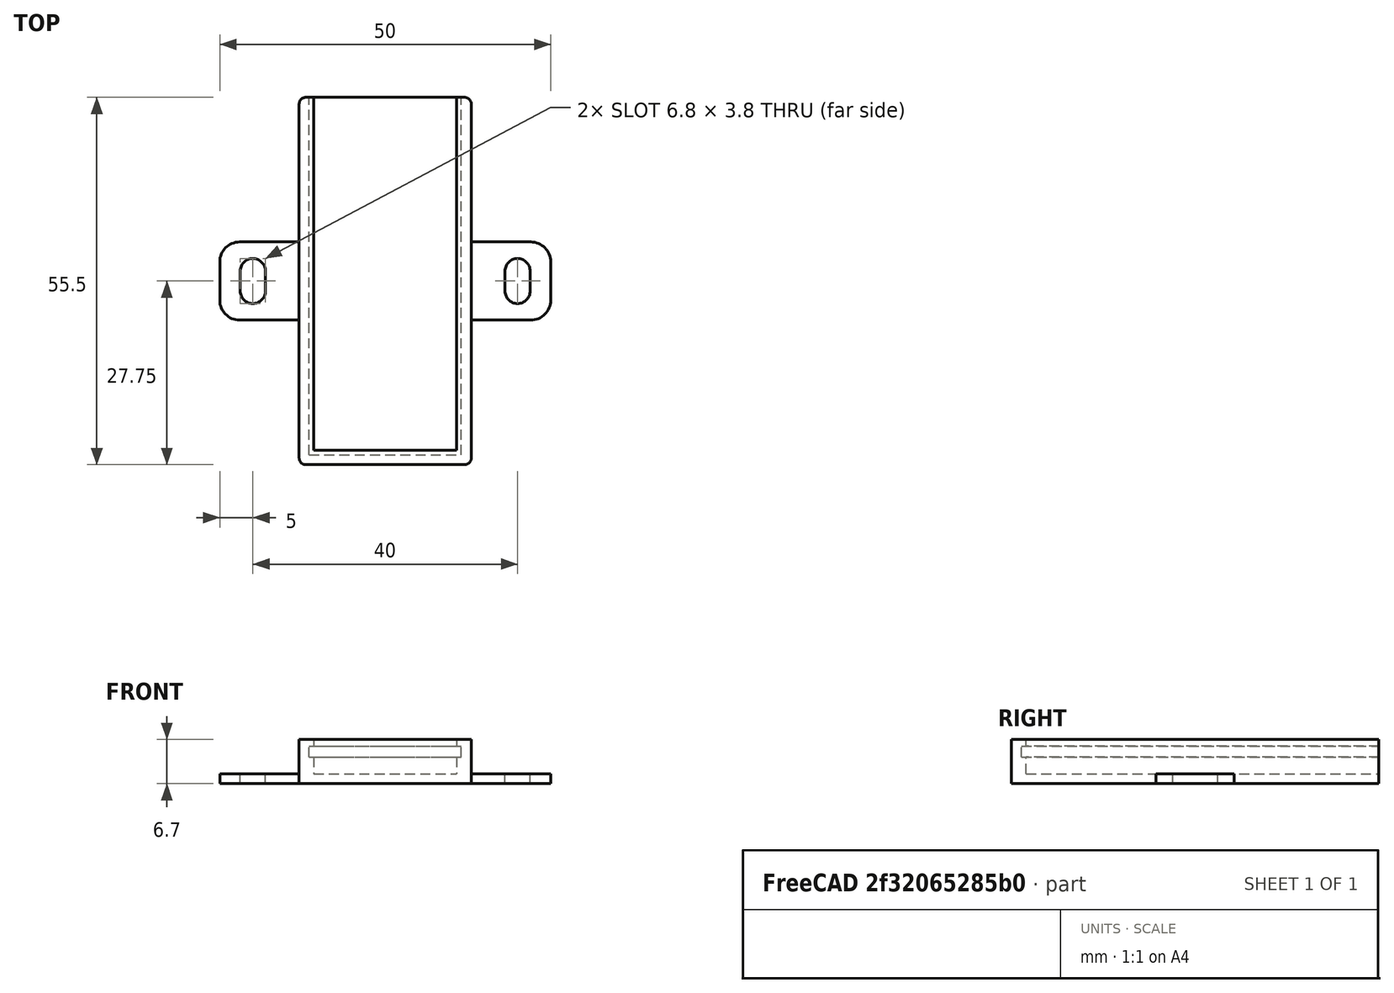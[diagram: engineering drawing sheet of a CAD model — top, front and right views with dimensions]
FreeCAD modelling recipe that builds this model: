
FCSTD DOCUMENT  (FreeCAD 0.19R)
Label: stm32_bluepill_2044l
License: FreeArt
LicenseURL: http://artlibre.org/licence/lal
objects: Part::Box×3, Part::MultiFuse×2, Part::Cut×2, App::Part×2, Spreadsheet::Sheet×1, Part::Fillet×1, Part::Feature×1
note: 9 computed .brp shape members not serialized (recipe doc carries the construction recipe); baked Part::Feature solids carry a one-line shape summary decoded from their .brp

FEATURE [Spreadsheet::Sheet] Spreadsheet  label="p"
  cells = A1=pcb_x; B1(pcb_x)=23; A2=pcb_y; B2(pcb_y)=54; A3=pcb_z; B3(pcb_z)=1.7; A4=pcb_under; B4(pcb_under)=2.5; A5=side_wall; B5(side_wall)=1.5; A6=pcb_side_lane; B6(pcb_side_lane)=0.7; A7=bottom_wall; B7(bottom_wall)=1.5; A8=pcb_above; B8(pcb_above)=1
FEATURE [Part::Box] Box  label="external cube"
  AttacherType = Attacher::AttachEngine3D
  Height = 6.7
  Length = 26
  Width = 55.5
  expr: Height = <<p>>.bottom_wall + <<p>>.pcb_under + <<p>>.pcb_z + <<p>>.pcb_above
  expr: Width = <<p>>.pcb_y + <<p>>.side_wall
  expr: Length = <<p>>.pcb_x + 2 * <<p>>.side_wall
FEATURE [Part::Box] Box006  label="internal cube"
  AttacherType = Attacher::AttachEngine3D
  Height = 5.2
  Length = 21.6
  Placement = pos=(2.2,2.2,1.5) rot=(0,0,1;0rad)
  Width = 54.1
  expr: .Placement.Base.y = <<p>>.side_wall + <<p>>.pcb_side_lane
  expr: .Placement.Base.x = <<p>>.side_wall + <<p>>.pcb_side_lane
  expr: .Placement.Base.z = <<p>>.bottom_wall
  expr: Height = <<p>>.pcb_under + <<p>>.pcb_z + <<p>>.pcb_above
  expr: Width = <<p>>.pcb_y - 2 * <<p>>.pcb_side_lane + <<p>>.side_wall
  expr: Length = <<p>>.pcb_x - 2 * <<p>>.pcb_side_lane
FEATURE [Part::Box] Box007  label="pcb extract cube"
  AttacherType = Attacher::AttachEngine3D
  Height = 1.7
  Length = 23
  Placement = pos=(1.5,1.5,4) rot=(0,0,1;0rad)
  Width = 54
  expr: .Placement.Base.y = <<p>>.side_wall
  expr: .Placement.Base.x = <<p>>.side_wall
  expr: Length = <<p>>.pcb_x
  expr: Width = <<p>>.pcb_y
  expr: .Placement.Base.z = <<p>>.bottom_wall + <<p>>.pcb_under
  expr: Height = <<p>>.pcb_z
FEATURE [Part::MultiFuse] Fusion  label="extract fusion"
  Shapes = -> [Box006,Box007]
FEATURE [Part::Fillet] Fillet  label="external fillet"
  Base = -> Box
  Edges = 4 edges r=1: [Edge1,Edge3,Edge5,Edge7]
FEATURE [Part::Feature] Cut003001  label="attach plane x dir001"
  Placement = pos=(-12,21.85,0) rot=(0,0,1;0rad)
  shape: bbox 50 x 11.8 x 1.5 mm, 18 faces (baked)
FEATURE [Part::MultiFuse] Fusion001  label="body fusion"
  Shapes = -> [Fillet,Cut003001]
FEATURE [Part::Cut] Cut  label="body cut"
  Base = -> Fusion001
  Tool = -> Fusion
FEATURE [App::Part] Part  label="pcb box part"
  Group = -> [Box,Fillet,Fusion001,Fusion,Box007,Box006,Cut]
  Origin = -> Origin
FEATURE [Part::Cut] Cut003002  label="body cut001"
  Base = -> Fillet
  Tool = -> Fusion
FEATURE [App::Part] Part001  label="pcb box part no attach"
  Group = -> [Cut003002]
  Origin = -> Origin001
